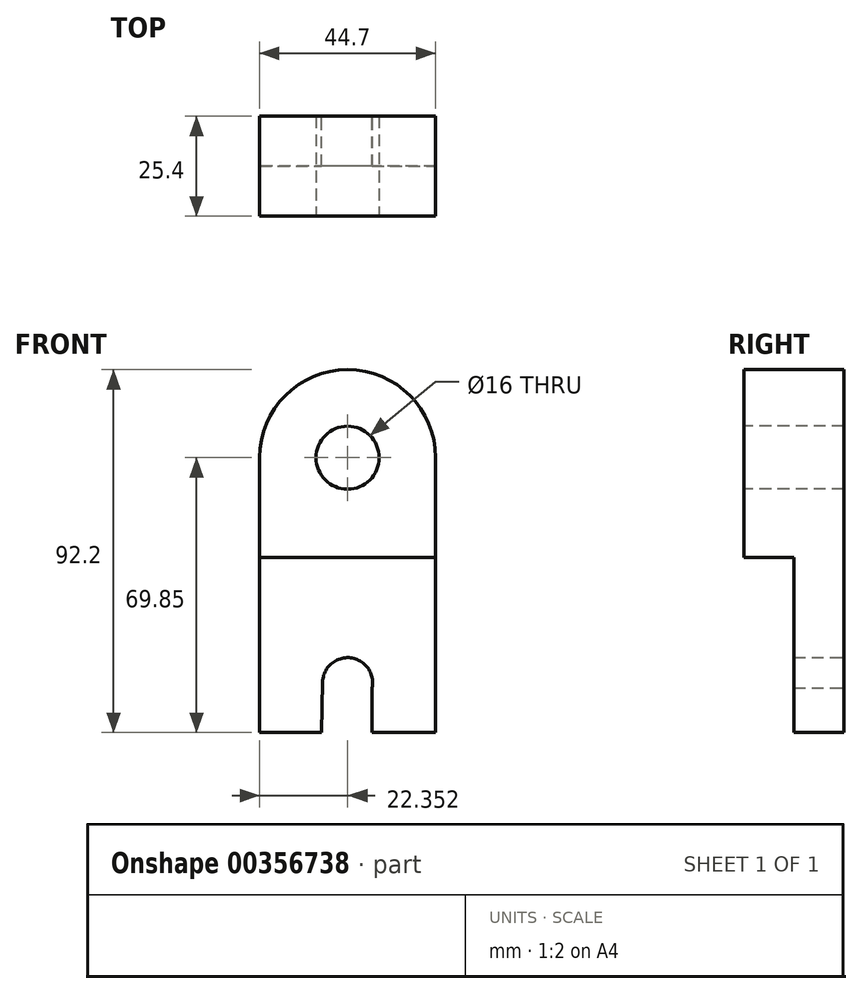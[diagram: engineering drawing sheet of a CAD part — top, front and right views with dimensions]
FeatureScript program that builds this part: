
annotation { "Feature Type Name" : "Feature", "Feature Type Description" : "" }
export const myFeature = defineFeature(function(context is Context, id is Id, definition is map)
    precondition{}
    {
        {
            var Q0;
            Q0=qCreatedBy(makeId("Front.planeOp"),FACE);
            var sketch = newSketch(context, id + "F0", { "sketchPlane" : qUnion([Q0])});
            skLineSegment(sketch, "E0", {"start": v(0, 0) * mm, "end": v(15.67, 0) * mm});
            skLineSegment(sketch, "E1", {"start": v(0, 0) * mm, "end": v(0, 69.85) * mm});
            skLineSegment(sketch, "E2", {"start": v(44.7, 0) * mm, "end": v(44.7, 69.85) * mm});
            skArc(sketch, "E3", {"start": v(44.7, 69.85) * mm, "mid": v(22.35, 92.2) * mm, "end": v(0, 69.85) * mm});
            skArc(sketch, "E4", {"start": v(28.56, 11.38) * mm, "mid": v(23.1, 19) * mm, "end": v(16, 12.86) * mm});
            skLineSegment(sketch, "E5", {"start": v(16, 12.86) * mm, "end": v(15.67, 0) * mm});
            skLineSegment(sketch, "E6", {"start": v(28.56, 14.02) * mm, "end": v(28.56, 0) * mm});
            skPoint(sketch, "E7.start.orphan", {"position": v(22.35, 0) * mm});
            skLineSegment(sketch, "E8.trimOffspring", {"start": v(28.56, 0) * mm, "end": v(44.7, 0) * mm});
            skSolve(sketch);
        }
        {
            var Q0;
            Q0=makeQuery(id+"F0.imprint","IMPRINT",FACE,{"disambiguationData":[TD([[makeQuery(id+"F0.imprint","IMPRINT",EDGE,{"derivedFrom":sQuery(id+"F0.wireOp",EDGE,"E0")}),1.0]])]});
            extrude(context, id + "F1", {"entities" : qUnion([Q0]), "depth" : 12.7 * mm});
        }
        {
            var Q0;
            Q0=makeQuery(id+"F1.opExtrude","CAP_FACE",FACE,{"disambiguationData":[OSD([sQuery(id+"F0.wireOp",EDGE,"E0"),sQuery(id+"F0.wireOp",EDGE,"E1"),sQuery(id+"F0.wireOp",EDGE,"E2"),sQuery(id+"F0.wireOp",EDGE,"E3"),sQuery(id+"F0.wireOp",EDGE,"E4"),sQuery(id+"F0.wireOp",EDGE,"E5"),sQuery(id+"F0.wireOp",EDGE,"E6"),sQuery(id+"F0.wireOp",EDGE,"E8.trimOffspring")])],"isStart":false});
            var sketch = newSketch(context, id + "F2", { "sketchPlane" : qUnion([Q0])});
            skLineSegment(sketch, "E9", {"start": v(0, 0) * mm, "end": v(0, 44.45) * mm});
            skLineSegment(sketch, "E10", {"start": v(2.1, 44.45) * mm, "end": v(44.7, 44.45) * mm});
            skLineSegment(sketch, "E11", {"start": v(2.1, 44.45) * mm, "end": v(0, 44.45) * mm});
            skSolve(sketch);
        }
        {
            var Q0;
            {var subQ3=sQuery(id+"F2.wireOp",EDGE,"E10");Q0=makeQuery(id+"F2.imprint","IMPRINT",FACE,{"disambiguationData":[TD([[makeQuery(id+"F2.imprint","IMPRINT",EDGE,{"derivedFrom":subQ3}),1.0]])]});}
            extrude(context, id + "F3", {"entities" : qUnion([Q0]), "operationType" : NewBodyOperationType.ADD, "depth" : 12.7 * mm});
        }
        {
            var Q0;
            Q0=makeQuery(id+"F3.opExtrude","CAP_FACE",FACE,{"disambiguationData":[OSD([sQuery(id+"F0.wireOp",EDGE,"E1"),sQuery(id+"F0.wireOp",EDGE,"E2"),sQuery(id+"F0.wireOp",EDGE,"E3"),sQuery(id+"F2.wireOp",EDGE,"E10"),sQuery(id+"F2.wireOp",EDGE,"E11")])],"isStart":false});
            var sketch = newSketch(context, id + "F4", { "sketchPlane" : qUnion([Q0])});
            skLineSegment(sketch, "E12", {"start": v(0, 44.45) * mm, "end": v(0, 69.85) * mm});
            skLineSegment(sketch, "E13", {"start": v(0, 69.85) * mm, "end": v(44.7, 69.85) * mm});
            skLineSegment(sketch, "E14", {"start": v(22.35, 69.85) * mm, "end": v(22.35, 44.45) * mm});
            skSolve(sketch);
        }
        {
            var Q0;
            Q0=sQuery(id+"F4.wireOp",VERTEX,"E14.start");
            var Q1;
            Q1=makeQuery(id+"F1.opExtrude","SWEPT_BODY",BODY,{"disambiguationData":[OSD([sQuery(id+"F0.wireOp",EDGE,"E0"),sQuery(id+"F0.wireOp",EDGE,"E1"),sQuery(id+"F0.wireOp",EDGE,"E2"),sQuery(id+"F0.wireOp",EDGE,"E3"),sQuery(id+"F0.wireOp",EDGE,"E4"),sQuery(id+"F0.wireOp",EDGE,"E5"),sQuery(id+"F0.wireOp",EDGE,"E6"),sQuery(id+"F0.wireOp",EDGE,"E8.trimOffspring")])]});
            hole(context, id + "F5", {"style" : HoleStyle.SIMPLE, "endStyle" : HoleEndStyle.THROUGH, "holeDiameter" : 16 * mm, "isTappedThrough" : true, "tappedDepth" : 12.7 * mm, "tapClearance" : 3, "startFromSketch" : true, "locations" : qUnion([Q0]), "scope" : qUnion([Q1])});
        }
    });
